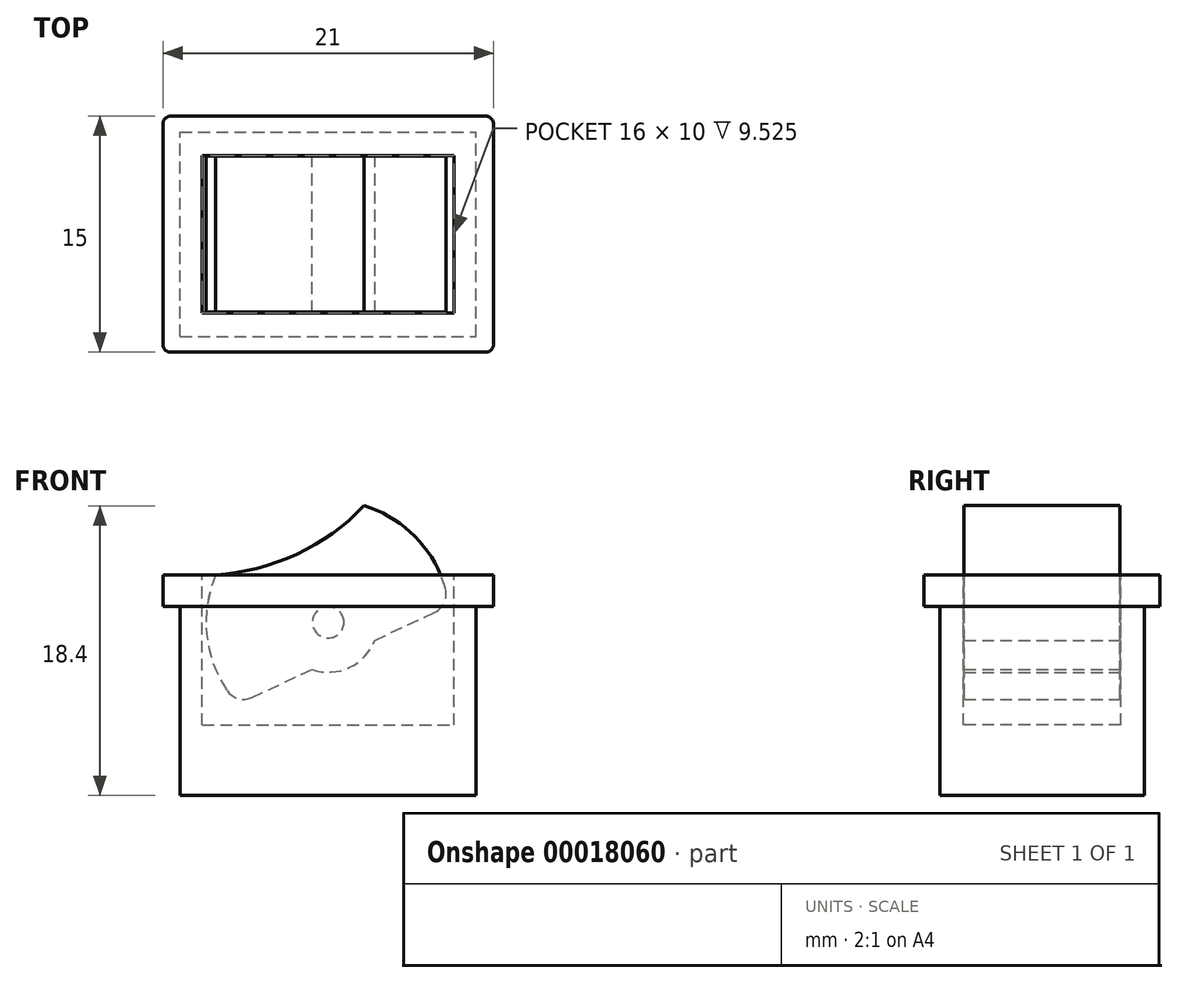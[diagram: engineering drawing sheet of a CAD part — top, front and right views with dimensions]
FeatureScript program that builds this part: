
annotation { "Feature Type Name" : "Feature", "Feature Type Description" : "" }
export const myFeature = defineFeature(function(context is Context, id is Id, definition is map)
    precondition{}
    {
        {
            var Q0;
            Q0=qCreatedBy(makeId("Top.planeOp"),FACE);
            var sketch = newSketch(context, id + "F0", { "sketchPlane" : qUnion([Q0])});
            skLineSegment(sketch, "E0.bottom", {"start": v(-10, -7.5) * mm, "end": v(10, -7.5) * mm});
            skLineSegment(sketch, "E0.top", {"start": v(-10, 7.5) * mm, "end": v(10, 7.5) * mm});
            skLineSegment(sketch, "E0.left", {"start": v(-10.5, -7) * mm, "end": v(-10.5, 7) * mm});
            skLineSegment(sketch, "E0.right", {"start": v(10.5, -7) * mm, "end": v(10.5, 7) * mm});
            skPoint(sketch, "E1.visualSharp", {"position": v(-10.5, -7.5) * mm});
            skArc(sketch, "E1.filletArc", {"start": v(-10.5, -7) * mm, "mid": v(-10.35, -7.35) * mm, "end": v(-10, -7.5) * mm});
            skPoint(sketch, "E2.visualSharp", {"position": v(-10.5, 7.5) * mm});
            skArc(sketch, "E2.filletArc", {"start": v(-10, 7.5) * mm, "mid": v(-10.35, 7.35) * mm, "end": v(-10.5, 7) * mm});
            skPoint(sketch, "E3.visualSharp", {"position": v(10.5, 7.5) * mm});
            skArc(sketch, "E3.filletArc", {"start": v(10.5, 7) * mm, "mid": v(10.35, 7.35) * mm, "end": v(10, 7.5) * mm});
            skPoint(sketch, "E4.visualSharp", {"position": v(10.5, -7.5) * mm});
            skArc(sketch, "E4.filletArc", {"start": v(10, -7.5) * mm, "mid": v(10.35, -7.35) * mm, "end": v(10.5, -7) * mm});
            skSolve(sketch);
        }
        {
            var Q0;
            Q0 = qSketchRegion(id + "F0", true);
            extrude(context, id + "F1", {"entities" : qUnion([Q0]), "depth" : 2 * mm});
        }
        {
            var Q0;
            Q0=makeQuery(id+"F1.opExtrude","CAP_FACE",FACE,{"disambiguationData":[OSD([sQuery(id+"F0.wireOp",EDGE,"E0.bottom"),sQuery(id+"F0.wireOp",EDGE,"E0.top"),sQuery(id+"F0.wireOp",EDGE,"E0.left"),sQuery(id+"F0.wireOp",EDGE,"E0.right"),sQuery(id+"F0.wireOp",EDGE,"E1.filletArc"),sQuery(id+"F0.wireOp",EDGE,"E2.filletArc"),sQuery(id+"F0.wireOp",EDGE,"E3.filletArc"),sQuery(id+"F0.wireOp",EDGE,"E4.filletArc")])],"isStart":true});
            var sketch = newSketch(context, id + "F2", { "sketchPlane" : qUnion([Q0])});
            skLineSegment(sketch, "E5.bottom", {"start": v(-9.4, 6.5) * mm, "end": v(9.4, 6.5) * mm});
            skLineSegment(sketch, "E5.top", {"start": v(-9.4, -6.5) * mm, "end": v(9.4, -6.5) * mm});
            skLineSegment(sketch, "E5.left", {"start": v(-9.4, 6.5) * mm, "end": v(-9.4, -6.5) * mm});
            skLineSegment(sketch, "E5.right", {"start": v(9.4, 6.5) * mm, "end": v(9.4, -6.5) * mm});
            skSolve(sketch);
        }
        {
            var Q0;
            Q0 = qSketchRegion(id + "F2", true);
            extrude(context, id + "F3", {"entities" : qUnion([Q0]), "operationType" : NewBodyOperationType.ADD, "depth" : 12 * mm});
        }
        {
            var Q0;
            Q0=makeQuery(id+"F1.opExtrude","CAP_FACE",FACE,{"disambiguationData":[OSD([sQuery(id+"F0.wireOp",EDGE,"E0.bottom"),sQuery(id+"F0.wireOp",EDGE,"E0.top"),sQuery(id+"F0.wireOp",EDGE,"E0.left"),sQuery(id+"F0.wireOp",EDGE,"E0.right"),sQuery(id+"F0.wireOp",EDGE,"E1.filletArc"),sQuery(id+"F0.wireOp",EDGE,"E2.filletArc"),sQuery(id+"F0.wireOp",EDGE,"E3.filletArc"),sQuery(id+"F0.wireOp",EDGE,"E4.filletArc")])],"isStart":false});
            var sketch = newSketch(context, id + "F4", { "sketchPlane" : qUnion([Q0])});
            skLineSegment(sketch, "E6.bottom", {"start": v(-8, 5) * mm, "end": v(8, 5) * mm});
            skLineSegment(sketch, "E6.top", {"start": v(-8, -5) * mm, "end": v(8, -5) * mm});
            skLineSegment(sketch, "E6.left", {"start": v(-8, 5) * mm, "end": v(-8, -5) * mm});
            skLineSegment(sketch, "E6.right", {"start": v(8, 5) * mm, "end": v(8, -5) * mm});
            skSolve(sketch);
        }
        {
            var Q0;
            Q0 = qSketchRegion(id + "F4", true);
            extrude(context, id + "F5", {"entities" : qUnion([Q0]), "operationType" : NewBodyOperationType.REMOVE, "oppositeDirection" : true, "depth" : 9.52 * mm});
        }
        {
            var Q0;
            Q0=qCreatedBy(makeId("Front.planeOp"),FACE);
            var sketch = newSketch(context, id + "F6", { "sketchPlane" : qUnion([Q0])});
            skCircle(sketch, "E7", {"center": v(0, -1) * mm, "radius": 1 * mm});
            skSolve(sketch);
        }
        {
            var Q0;
            Q0 = qSketchRegion(id + "F6", true);
            extrude(context, id + "F7", {"entities" : qUnion([Q0]), "operationType" : NewBodyOperationType.ADD, "endBound" : BoundingType.SYMMETRIC, "depth" : 11 * mm});
        }
        {
            var Q0;
            Q0=qCreatedBy(makeId("Front.planeOp"),FACE);
            var sketch = newSketch(context, id + "F8", { "sketchPlane" : qUnion([Q0])});
            skArc(sketch, "E8", {"start": v(-1.03, -4) * mm, "mid": v(1.34, -3.88) * mm, "end": v(2.96, -2.14) * mm});
            skArc(sketch, "E9", {"start": v(-7.14, 2) * mm, "mid": v(-7.71, -1.76) * mm, "end": v(-6.42, -5.34) * mm});
            skLineSegment(sketch, "E10", {"start": v(0, -1) * mm, "end": v(-8.05, 16.27) * mm, "construction": true});
            skArc(sketch, "E11", {"start": v(-7.14, 2) * mm, "mid": v(-2.01, 3.32) * mm, "end": v(2.29, 6.4) * mm});
            skLineSegment(sketch, "E12", {"start": v(-4.83, -5.78) * mm, "end": v(-1.03, -4) * mm});
            skArc(sketch, "E13.trimOffspring", {"start": v(7.45, 1.13) * mm, "mid": v(5.54, 4.42) * mm, "end": v(2.29, 6.4) * mm});
            skLineSegment(sketch, "E14.trimOffspring", {"start": v(2.96, -2.14) * mm, "end": v(6.77, -0.37) * mm});
            skPoint(sketch, "E15.visualSharp", {"position": v(-5.75, -6.2) * mm});
            skArc(sketch, "E15.filletArc", {"start": v(-6.42, -5.34) * mm, "mid": v(-5.71, -5.85) * mm, "end": v(-4.83, -5.78) * mm});
            skPoint(sketch, "E16.visualSharp", {"position": v(7.68, 0.06) * mm});
            skArc(sketch, "E16.filletArc", {"start": v(6.77, -0.37) * mm, "mid": v(7.39, 0.26) * mm, "end": v(7.45, 1.13) * mm});
            skSolve(sketch);
        }
        {
            var Q0;
            Q0 = qSketchRegion(id + "F8", true);
            extrude(context, id + "F9", {"entities" : qUnion([Q0]), "operationType" : NewBodyOperationType.ADD, "endBound" : BoundingType.SYMMETRIC, "depth" : 9.9 * mm});
        }
    });
